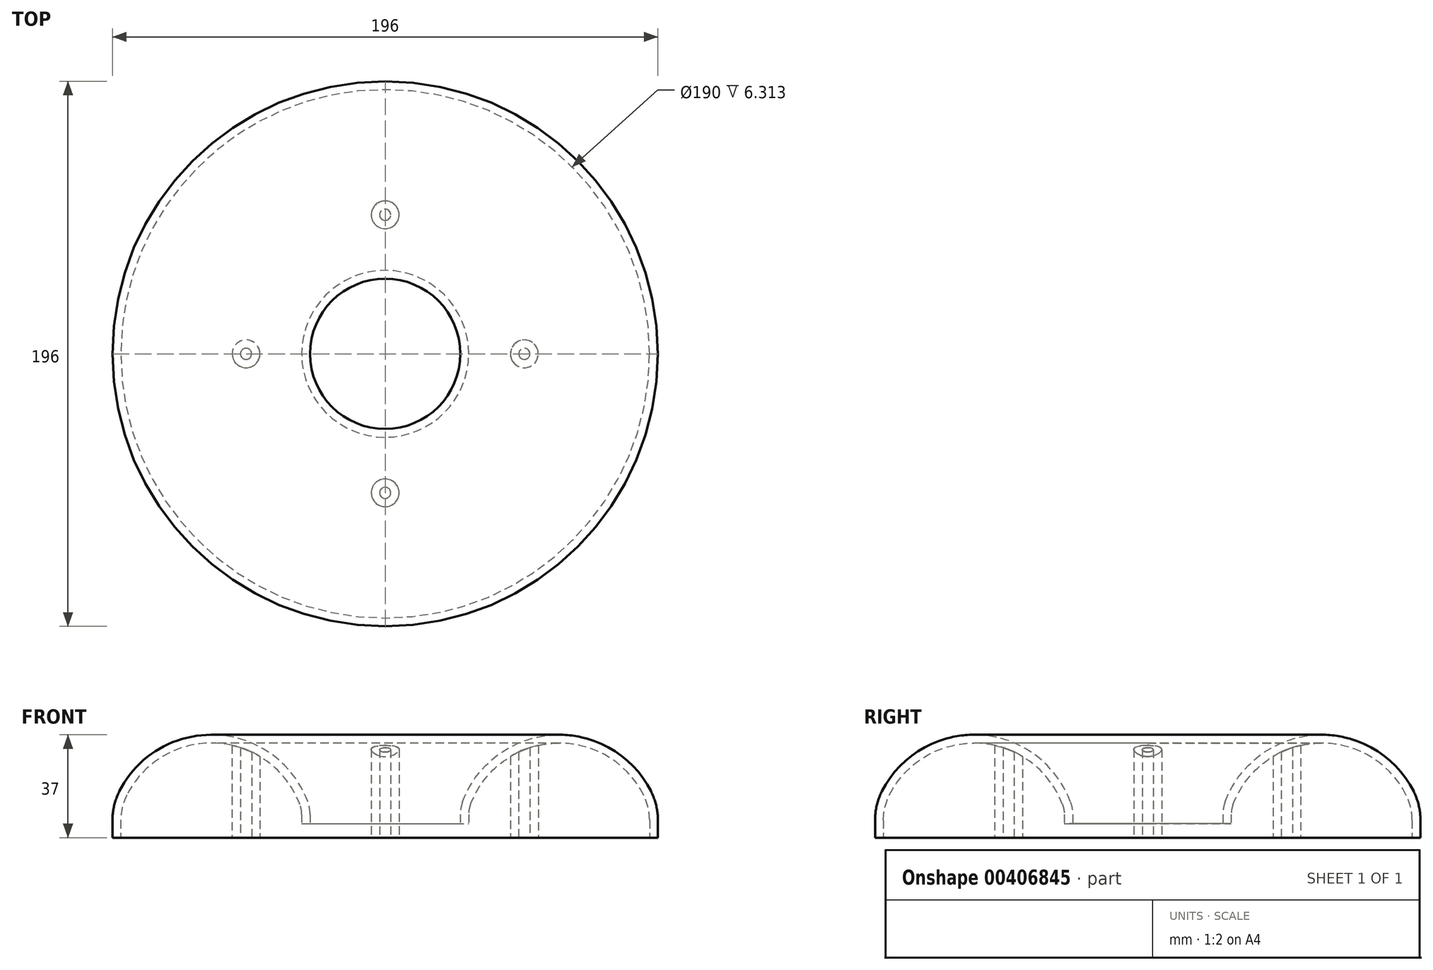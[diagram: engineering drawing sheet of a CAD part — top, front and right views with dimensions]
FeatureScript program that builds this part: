
annotation { "Feature Type Name" : "Feature", "Feature Type Description" : "" }
export const myFeature = defineFeature(function(context is Context, id is Id, definition is map)
    precondition{}
    {
        {
            var Q0;
            Q0=qCreatedBy(makeId("Front.planeOp"),FACE);
            var sketch = newSketch(context, id + "F0", { "sketchPlane" : qUnion([Q0])});
            skArc(sketch, "E0", {"start": v(-30.63, 11.85) * mm, "mid": v(-60.6, 33.95) * mm, "end": v(-92.85, 15.33) * mm});
            skLineSegment(sketch, "E1", {"start": v(-95, 6.31) * mm, "end": v(-95, 0) * mm});
            skPoint(sketch, "E2.visualSharp", {"position": v(-95, 10) * mm});
            skArc(sketch, "E2.filletArc", {"start": v(-92.85, 15.33) * mm, "mid": v(-94.46, 10.95) * mm, "end": v(-95, 6.31) * mm});
            skLineSegment(sketch, "E3", {"start": v(-30, 8.36) * mm, "end": v(-30, 5) * mm});
            skPoint(sketch, "E4.visualSharp", {"position": v(-30, 10) * mm});
            skArc(sketch, "E4.filletArc", {"start": v(-30, 8.36) * mm, "mid": v(-30.16, 10.13) * mm, "end": v(-30.63, 11.85) * mm});
            skLineSegment(sketch, "E5.0", {"start": v(-98, 6.31) * mm, "end": v(-98, 0) * mm});
            skLineSegment(sketch, "E5.1", {"start": v(-27, 8.36) * mm, "end": v(-27, 5) * mm});
            skArc(sketch, "E5.2", {"start": v(-27, 8.36) * mm, "mid": v(-27.2, 10.66) * mm, "end": v(-27.81, 12.9) * mm});
            skArc(sketch, "E5.3", {"start": v(-27.81, 12.9) * mm, "mid": v(-60.43, 36.95) * mm, "end": v(-95.53, 16.68) * mm});
            skArc(sketch, "E5.4", {"start": v(-95.53, 16.68) * mm, "mid": v(-97.37, 11.64) * mm, "end": v(-98, 6.31) * mm});
            skLineSegment(sketch, "E6", {"start": v(-30, 5) * mm, "end": v(-27, 5) * mm});
            skLineSegment(sketch, "E7", {"start": v(-98, 0) * mm, "end": v(-95, 0) * mm});
            skLineSegment(sketch, "E8", {"start": v(0, 0) * mm, "end": v(0, 68.83) * mm, "construction": true});
            skSolve(sketch);
        }
        {
            var Q0;
            Q0=makeQuery(id+"F0.imprint","IMPRINT",FACE,{"disambiguationData":[TD([[makeQuery(id+"F0.imprint","IMPRINT",EDGE,{"derivedFrom":sQuery(id+"F0.wireOp",EDGE,"E0")}),-1.0]])]});
            var Q1;
            Q1=sQuery(id+"F0.wireOp",EDGE,"E8");
            revolve(context, id + "F1", {"entities" : qUnion([Q0]), "axis" : qUnion([Q1]), "revolveType" : RevolveType.FULL});
        }
        {
            var Q0;
            Q0=makeQuery(id+"F1.opRevolve","SWEPT_FACE",FACE,{"disambiguationData":[OSD([sQuery(id+"F0.wireOp",EDGE,"E7")])]});
            var sketch = newSketch(context, id + "F2", { "sketchPlane" : qUnion([Q0])});
            skCircle(sketch, "E9", {"center": v(-50, 0) * mm, "radius": 5 * mm});
            skCircle(sketch, "E10", {"center": v(-50, 0) * mm, "radius": 2 * mm});
            skCircle(sketch, "E11.1.0", {"center": v(0, -50) * mm, "radius": 5 * mm});
            skCircle(sketch, "E11.1.1", {"center": v(0, -50) * mm, "radius": 2 * mm});
            skCircle(sketch, "E11.2.0", {"center": v(50, 0) * mm, "radius": 5 * mm});
            skCircle(sketch, "E11.2.1", {"center": v(50, 0) * mm, "radius": 2 * mm});
            skCircle(sketch, "E11.3.0", {"center": v(0, 50) * mm, "radius": 5 * mm});
            skCircle(sketch, "E11.3.1", {"center": v(0, 50) * mm, "radius": 2 * mm});
            skPoint(sketch, "E11.center", {"position": v(0, 0) * mm});
            skSolve(sketch);
        }
        {
            var Q0;
            Q0 = qSketchRegion(id + "F2", true);
            extrude(context, id + "F3", {"entities" : qUnion([Q0]), "operationType" : NewBodyOperationType.ADD, "endBound" : BoundingType.UP_TO_NEXT, "oppositeDirection" : true, "depth" : 25 * mm});
        }
    });
